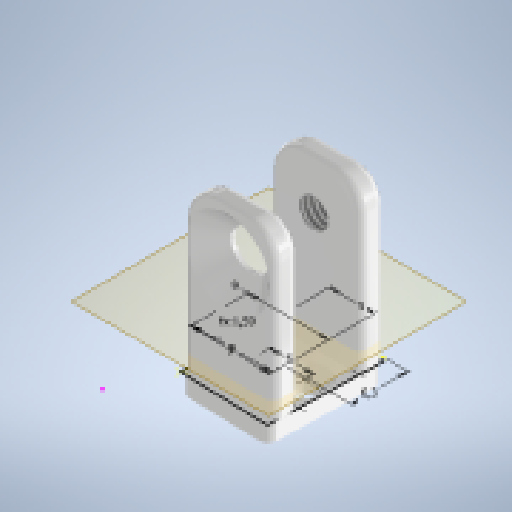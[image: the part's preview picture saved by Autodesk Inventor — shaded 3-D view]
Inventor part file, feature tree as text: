
AUTODESK INVENTOR PART (.ipt)
format: ipt  version: 2025 (Build 290162010, 162A)  size: 310,272 bytes
history: native  units: mm
features: sketch x4, hole x3, extrude x2, fillet x2, plane x1
ambient origin geometry x8: Origin, YZ Plane, XZ Plane, XY Plane, X Axis, Y Axis, Z Axis, Center Point
bodies: Volumenkörper1 (feature_tree)
feature tree (12):
  extrude  "Extrusion1"  Depth=3.0mm
  fillet  "Rundung1"  Radius=3.0mm
  hole  "Bohrung1"  [1 undecoded]
  plane  "Arbeitsebene1"
  sketch  "Skizze4"  dims[d7=3.0mm]
  extrude  "Extrusion3"  Depth=1.0mm
  hole  "Bohrung2"  [1 undecoded]
  hole  "Bohrung3"  [1 undecoded]
  fillet  "Rundung2"  Radius=5.0mm
  sketch  "Skizze1"  dims[d0=10.0mm d1=3.0mm d2=3.0mm]
  sketch  "Skizze2"  dims[d3=6.6mm d5=18.0mm d6=0.0mm]
  sketch  "Skizze5"  dims[d8=4.3mm d9=8.0mm d10=9.4mm d11=14.0mm d12=90.0deg d13=11.8mm d14=20.594885mm d19=2.0mm d20=8.0mm d21=5.0mm d22=2.0mm d23=90.0deg d24=8.0mm d25=20.594885mm d26=3.242mm d27=8.0mm d28=4.0mm d29=2.0mm d30=90.0deg d31=5.0mm d32=20.594885mm d34=5.0mm d35=9.0mm d36=6.3mm d37=5.0mm d38=9.0mm d40=9.0mm d41=0.277101mm d42=2.0mm d43=0.0mm d44=1.0mm]
note: 3 required parameter values undecoded (feature->parameter linkage not recoverable at this tier; creation-order binding heuristic only, values carry confidence <= 0.55)
